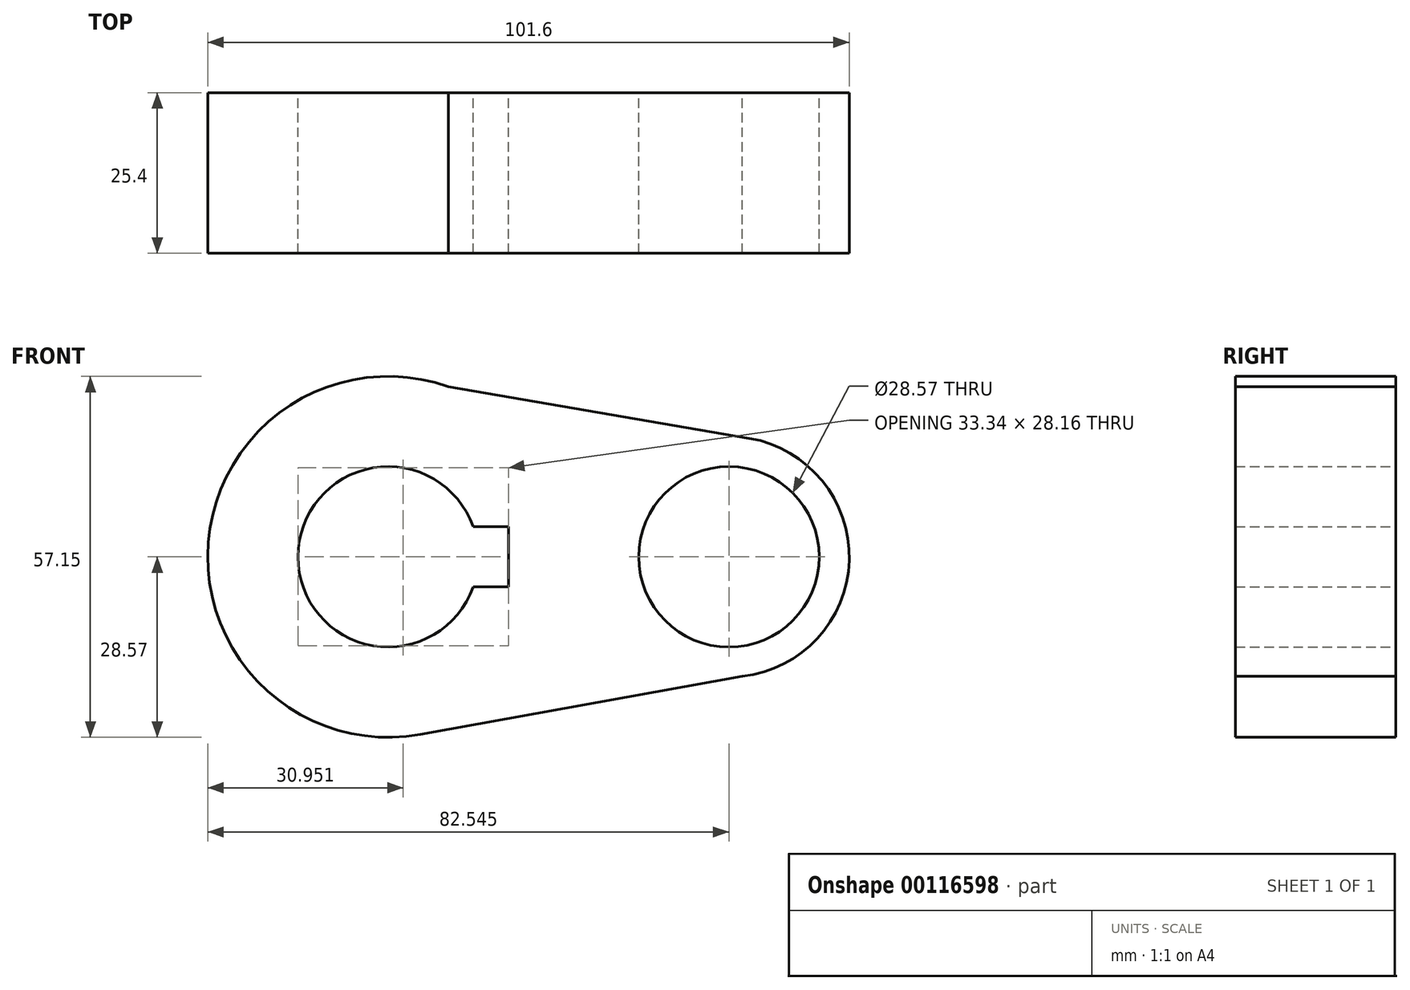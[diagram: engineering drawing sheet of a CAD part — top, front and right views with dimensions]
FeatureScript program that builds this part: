
annotation { "Feature Type Name" : "Feature", "Feature Type Description" : "" }
export const myFeature = defineFeature(function(context is Context, id is Id, definition is map)
    precondition{}
    {
        {
            var Q0;
            Q0=qCreatedBy(makeId("Front.planeOp"),FACE);
            var sketch = newSketch(context, id + "F0", { "sketchPlane" : qUnion([Q0])});
            skCircle(sketch, "E0", {"center": v(0, 0) * mm, "radius": 28.57 * mm});
            skCircle(sketch, "E1", {"center": v(53.98, 0) * mm, "radius": 19.05 * mm});
            skLineSegment(sketch, "E2", {"start": v(0, 28.58) * mm, "end": v(57.2, 18.78) * mm});
            skLineSegment(sketch, "E3", {"start": v(56.07, -18.93) * mm, "end": v(5.07, -28.12) * mm});
            skCircle(sketch, "E4", {"center": v(0, 0) * mm, "radius": 14.29 * mm});
            skCircle(sketch, "E5", {"center": v(53.98, 0) * mm, "radius": 14.29 * mm});
            skLineSegment(sketch, "E6.bottom", {"start": v(19.05, -4.76) * mm, "end": v(-19.05, -4.76) * mm});
            skLineSegment(sketch, "E6.top", {"start": v(19.05, 4.76) * mm, "end": v(-19.05, 4.76) * mm});
            skLineSegment(sketch, "E6.left", {"start": v(19.05, -4.76) * mm, "end": v(19.05, 4.76) * mm});
            skLineSegment(sketch, "E6.right", {"start": v(-19.05, -4.76) * mm, "end": v(-19.05, 4.76) * mm});
            skSolve(sketch);
        }
        {
            var Q0;
            Q0 = qSketchRegion(id + "F0", true);
            var Q1;
            {var subQ5=sQuery(id+"F0.wireOp",EDGE,"E6.right");Q1=makeQuery(id+"F0.imprint","IMPRINT",FACE,{"disambiguationData":[TD([[makeQuery(id+"F0.imprint","IMPRINT",EDGE,{"derivedFrom":subQ5}),-1.0]])]});}
            extrude(context, id + "F1", {"entities" : qUnion([Q0, Q1]), "depth" : 25.4 * mm});
        }
    });
